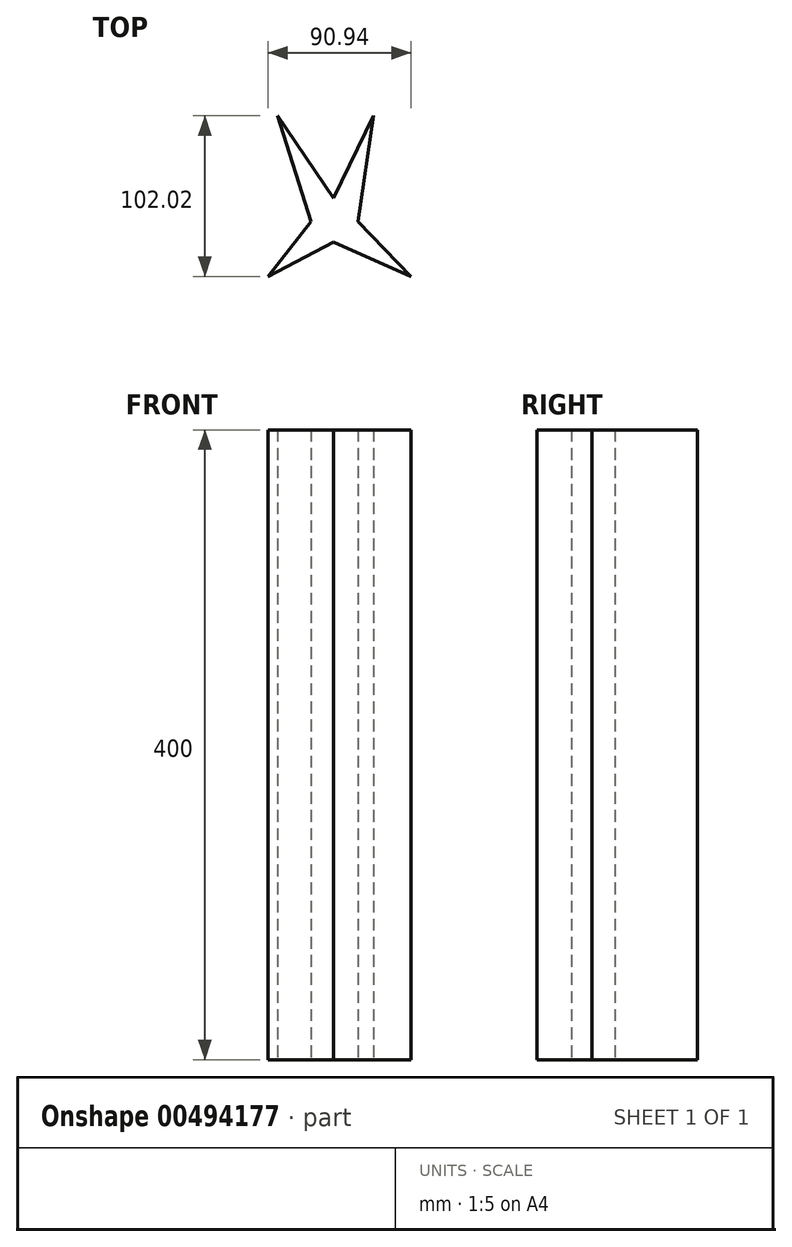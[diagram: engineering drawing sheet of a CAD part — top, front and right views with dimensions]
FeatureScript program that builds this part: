
annotation { "Feature Type Name" : "Feature", "Feature Type Description" : "" }
export const myFeature = defineFeature(function(context is Context, id is Id, definition is map)
    precondition{}
    {
        {
            var Q0;
            Q0=qCreatedBy(makeId("Top.planeOp"),FACE);
            var sketch = newSketch(context, id + "F0", { "sketchPlane" : qUnion([Q0])});
            skLineSegment(sketch, "E0", {"start": v(0, 0) * mm, "end": v(-35.56, 52.32) * mm});
            skLineSegment(sketch, "E1", {"start": v(-35.56, 52.32) * mm, "end": v(-14.28, -14.72) * mm});
            skLineSegment(sketch, "E2", {"start": v(-14.28, -14.72) * mm, "end": v(-41.68, -49.7) * mm});
            skLineSegment(sketch, "E3", {"start": v(-41.68, -49.7) * mm, "end": v(0, -27.84) * mm});
            skLineSegment(sketch, "E4", {"start": v(0, 0) * mm, "end": v(25.36, 52.32) * mm});
            skLineSegment(sketch, "E5", {"start": v(25.36, 52.32) * mm, "end": v(15.74, -14.72) * mm});
            skLineSegment(sketch, "E6", {"start": v(15.74, -14.72) * mm, "end": v(49.26, -49.7) * mm});
            skLineSegment(sketch, "E7", {"start": v(0, -27.84) * mm, "end": v(49.26, -49.7) * mm});
            skSolve(sketch);
        }
        {
            var Q0;
            Q0=makeQuery(id+"F0.imprint","IMPRINT",FACE,{"disambiguationData":[TD([[makeQuery(id+"F0.imprint","IMPRINT",EDGE,{"derivedFrom":sQuery(id+"F0.wireOp",EDGE,"E0")}),1.0]])]});
            extrude(context, id + "F1", {"entities" : qUnion([Q0]), "endBound" : BoundingType.SYMMETRIC, "depth" : 400 * mm});
        }
    });
